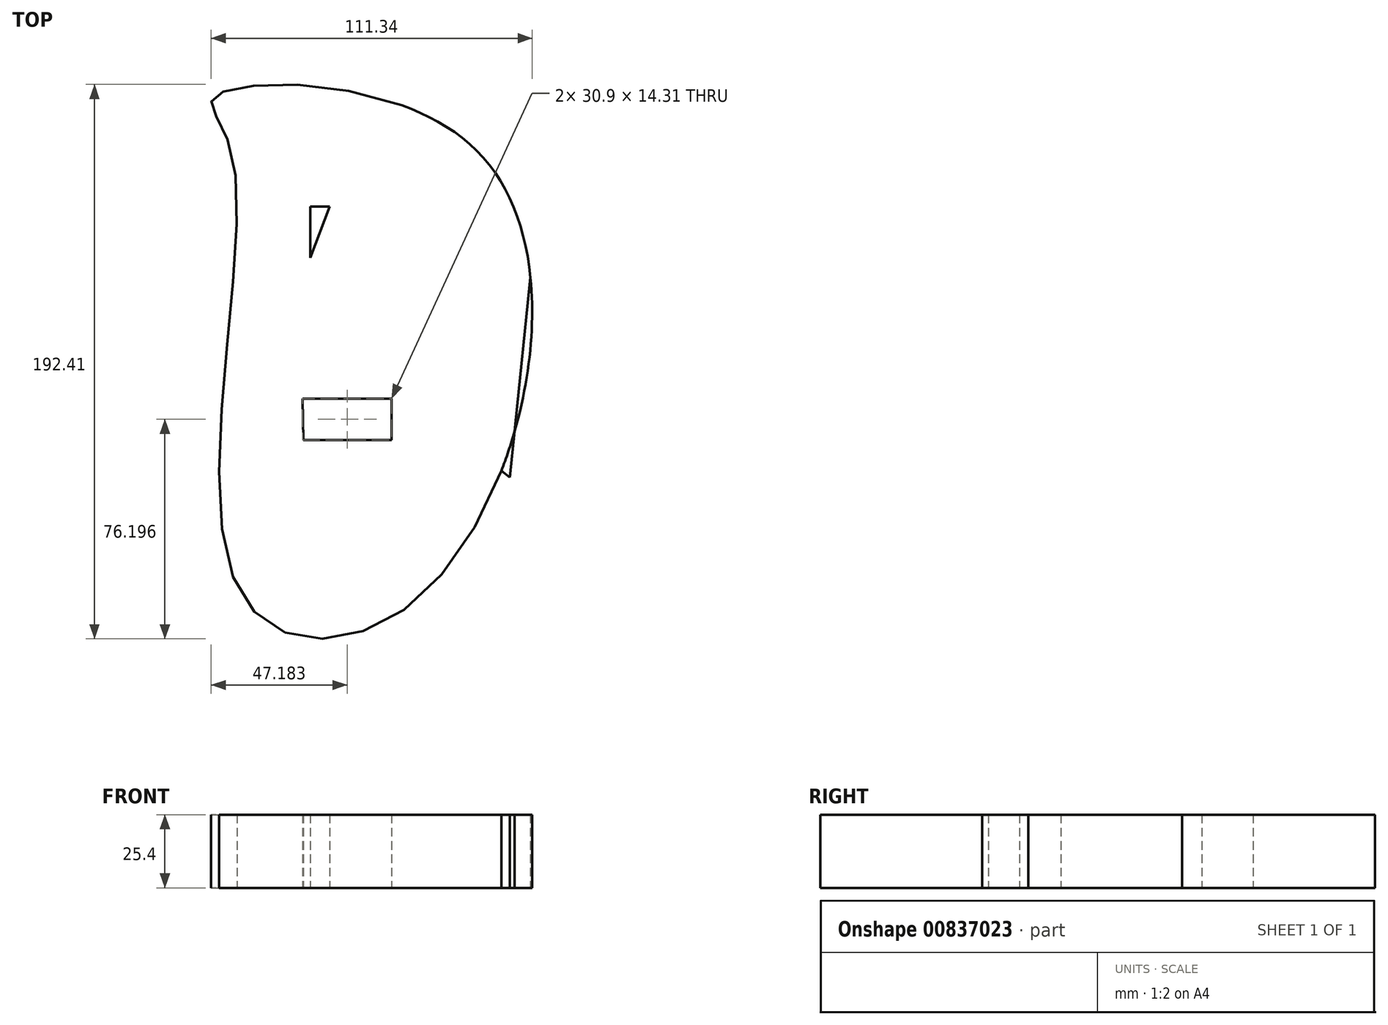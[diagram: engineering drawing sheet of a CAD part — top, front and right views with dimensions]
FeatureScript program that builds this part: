
annotation { "Feature Type Name" : "Feature", "Feature Type Description" : "" }
export const myFeature = defineFeature(function(context is Context, id is Id, definition is map)
    precondition{}
    {
        {
            var Q0;
            Q0=qCreatedBy(makeId("Top.planeOp"),FACE);
            var sketch = newSketch(context, id + "F0", { "sketchPlane" : qUnion([Q0])});
            skFitSpline(sketch, "E0", {"points": [v(-66.6, 75.23) * mm, v(-63.98, -76.55) * mm, v(0, -76.81) * mm, v(19.8, 74.97) * mm, v(-72.84, 95.5) * mm, v(-66.6, 75.23) * mm]});
            skLineSegment(sketch, "E1", {"start": v(-41.99, -23.75) * mm, "end": v(-11.34, -23.75) * mm});
            skLineSegment(sketch, "E2", {"start": v(-11.34, -23.75) * mm, "end": v(-11.34, -9.44) * mm});
            skLineSegment(sketch, "E3", {"start": v(-11.34, -9.44) * mm, "end": v(-42.24, -9.44) * mm});
            skLineSegment(sketch, "E4", {"start": v(-42.24, -9.44) * mm, "end": v(-41.99, -23.75) * mm});
            skLineSegment(sketch, "E5", {"start": v(-20.06, 39.49) * mm, "end": v(-13.15, 39.49) * mm});
            skLineSegment(sketch, "E6", {"start": v(-7.8, 92.38) * mm, "end": v(-7.2, 94.2) * mm});
            skLineSegment(sketch, "E7", {"start": v(-39.57, 77.47) * mm, "end": v(-39.57, 77.47) * mm});
            skLineSegment(sketch, "E8", {"start": v(-39.57, 77.47) * mm, "end": v(-42.82, 69.74) * mm});
            skPoint(sketch, "E9.start.orphan", {"position": v(-39.57, 39.49) * mm});
            skLineSegment(sketch, "E10", {"start": v(-32.13, 62.76) * mm, "end": v(-39.57, 77.47) * mm});
            skLineSegment(sketch, "E11", {"start": v(-32.13, 59.08) * mm, "end": v(-39.57, 39.49) * mm});
            skLineSegment(sketch, "E12", {"start": v(-39.57, 39.49) * mm, "end": v(-13.15, 39.49) * mm});
            skLineSegment(sketch, "E13", {"start": v(-11.38, 57.22) * mm, "end": v(-39.57, 57.22) * mm});
            skLineSegment(sketch, "E14", {"start": v(-39.57, 57.22) * mm, "end": v(-39.57, 39.49) * mm});
            skLineSegment(sketch, "E15", {"start": v(26.68, -34.51) * mm, "end": v(26.68, -34.51) * mm});
            skLineSegment(sketch, "E16", {"start": v(26.68, -34.51) * mm, "end": v(29.66, -36.73) * mm});
            skLineSegment(sketch, "E17", {"start": v(29.66, -36.73) * mm, "end": v(38.1, 45.27) * mm});
            skLineSegment(sketch, "E18", {"start": v(38.1, 45.27) * mm, "end": v(53.58, 71.39) * mm});
            skLineSegment(sketch, "E19", {"start": v(53.58, 71.39) * mm, "end": v(47.95, -93.17) * mm});
            skLineSegment(sketch, "E20", {"start": v(47.95, -93.17) * mm, "end": v(72.35, 107.36) * mm});
            skLineSegment(sketch, "E21", {"start": v(72.35, 107.36) * mm, "end": v(61.03, -70.2) * mm});
            skLineSegment(sketch, "E22", {"start": v(61.03, -70.2) * mm, "end": v(71.44, -92.2) * mm});
            skLineSegment(sketch, "E23", {"start": v(71.44, -92.2) * mm, "end": v(84.44, 126.3) * mm});
            skLineSegment(sketch, "E24", {"start": v(84.44, 126.3) * mm, "end": v(11.58, 68.22) * mm, "construction": true});
            skLineSegment(sketch, "E25", {"start": v(11.58, 68.22) * mm, "end": v(21.65, -46.08) * mm, "construction": true});
            skSolve(sketch);
        }
        {
            var Q0;
            Q0=makeQuery(id+"F0.imprint","IMPRINT",FACE,{"disambiguationData":[TD([[makeQuery(id+"F0.imprint","IMPRINT",EDGE,{"derivedFrom":sQuery(id+"F0.wireOp",EDGE,"E1")}),-1.0]])]});
            var sketch = newSketch(context, id + "F1", { "sketchPlane" : qUnion([Q0])});
            skSolve(sketch);
        }
        {
            var Q0;
            Q0=makeQuery(id+"F1.imprint","IMPRINT",FACE,{"disambiguationData":[TD([[makeQuery(id+"F1.imprint","IMPRINT",EDGE,{"derivedFrom":makeQuery(id+"F0.imprint","IMPRINT",EDGE,{"derivedFrom":sQuery(id+"F0.wireOp",EDGE,"E1")})}),-1.0]])]});
            var Q1;
            Q1 = qSketchRegion(id + "F0", true);
            extrude(context, id + "F2", {"entities" : qUnion([Q0, Q1]), "depth" : 25.4 * mm, "offsetDistance" : 25.4 * mm});
        }
    });
